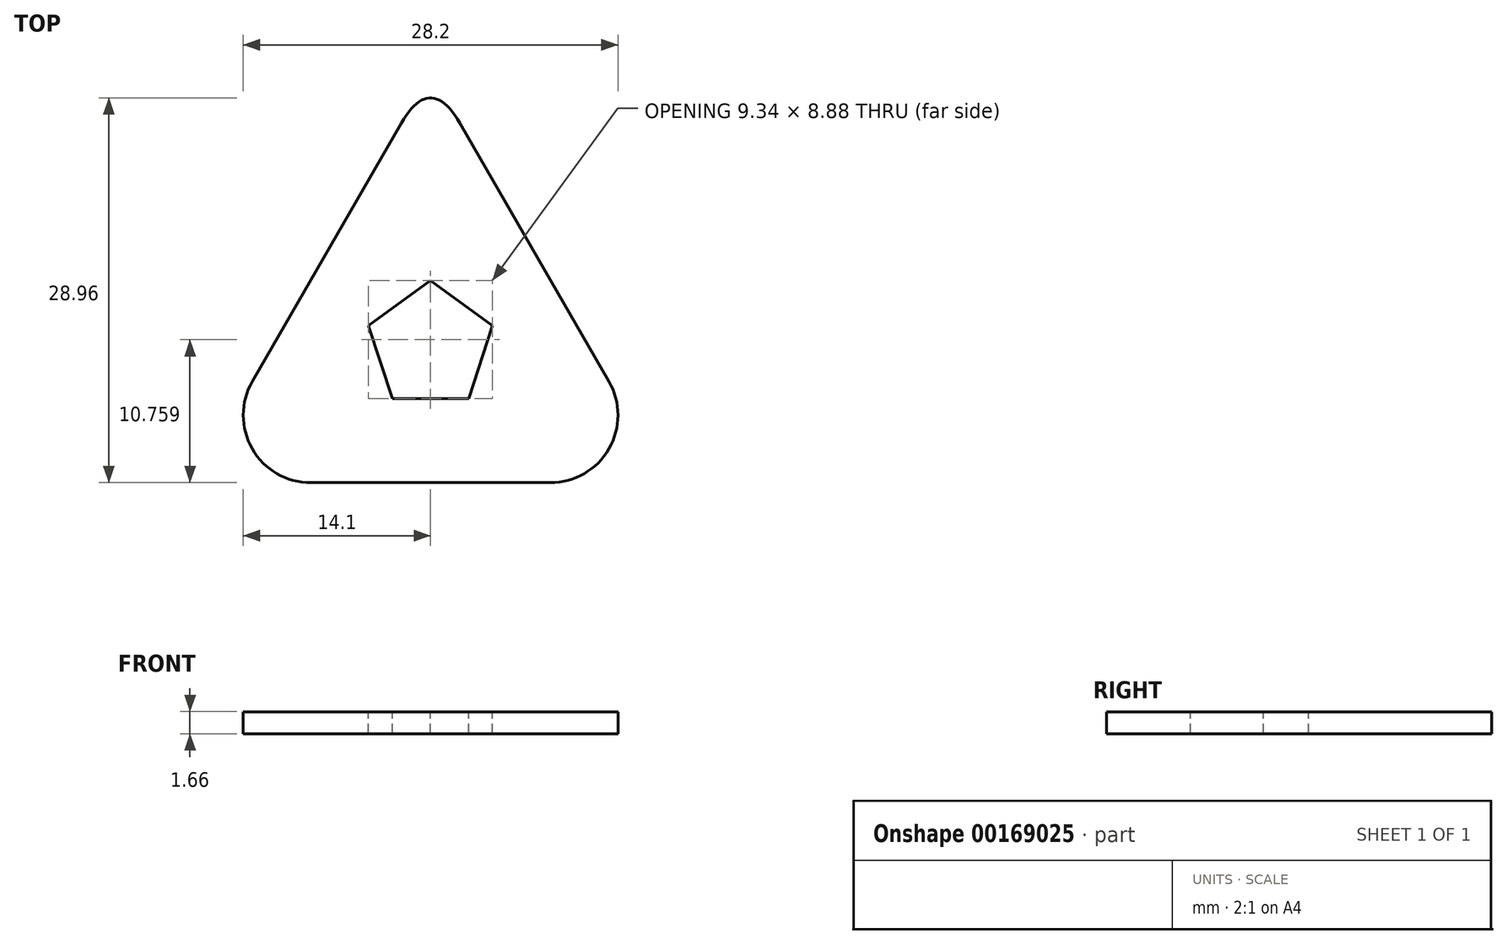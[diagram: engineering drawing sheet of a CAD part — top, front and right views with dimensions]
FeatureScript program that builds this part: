
annotation { "Feature Type Name" : "Feature", "Feature Type Description" : "" }
export const myFeature = defineFeature(function(context is Context, id is Id, definition is map)
    precondition{}
    {
        {
            var Q0;
            Q0=qCreatedBy(makeId("Top.planeOp"),FACE);
            var sketch = newSketch(context, id + "F0", { "sketchPlane" : qUnion([Q0])});
            skCircle(sketch, "E0.cCircle", {"center": v(0, 0) * mm, "radius": 20.58 * mm, "construction": true});
            skLineSegment(sketch, "E0.0", {"start": v(0, 20.58) * mm, "end": v(17.82, -10.29) * mm});
            skLineSegment(sketch, "E0.1", {"start": v(17.82, -10.29) * mm, "end": v(-17.82, -10.29) * mm});
            skLineSegment(sketch, "E0.2", {"start": v(-17.82, -10.29) * mm, "end": v(0, 20.58) * mm});
            skSolve(sketch);
        }
        {
            var Q0;
            Q0=makeQuery(id+"F0.imprint","IMPRINT",FACE,{"disambiguationData":[TD([[makeQuery(id+"F0.imprint","IMPRINT",EDGE,{"derivedFrom":sQuery(id+"F0.wireOp",EDGE,"E0.0")}),-1.0]])]});
            var Q1;
            Q1=sQuery(id+"F0.wireOp",EDGE,"E0.1");
            var Q2;
            Q2=sQuery(id+"F0.wireOp",EDGE,"E0.0");
            var Q3;
            Q3=sQuery(id+"F0.wireOp",EDGE,"E0.2");
            extrude(context, id + "F1", {"entities" : qUnion([Q0]), "surfaceEntities" : qUnion([Q1, Q2, Q3]), "depth" : 1.66 * mm});
        }
        {
            var Q0;
            Q0=makeQuery(id+"F1.opExtrude","SWEPT_EDGE",EDGE,{"disambiguationData":[OSD([sQuery(id+"F0.wireOp",EDGE,"E0.0"),sQuery(id+"F0.wireOp",EDGE,"E0.2")])]});
            fillet(context, id + "F2", {"entities" : qUnion([Q0]), "radius" : 2.54 * mm, "tangentPropagation" : true, "rho" : 0.5, "crossSection" : FilletCrossSection.CONIC, "allowEdgeOverflow" : false});
        }
        {
            var Q0;
            Q0=makeQuery(id+"F1.opExtrude","SWEPT_EDGE",EDGE,{"disambiguationData":[OSD([sQuery(id+"F0.wireOp",EDGE,"E0.1"),sQuery(id+"F0.wireOp",EDGE,"E0.2")])]});
            fillet(context, id + "F3", {"entities" : qUnion([Q0]), "radius" : 5.08 * mm, "tangentPropagation" : true, "allowEdgeOverflow" : false});
        }
        {
            var Q0;
            Q0=makeQuery(id+"F1.opExtrude","SWEPT_EDGE",EDGE,{"disambiguationData":[OSD([sQuery(id+"F0.wireOp",EDGE,"E0.0"),sQuery(id+"F0.wireOp",EDGE,"E0.1")])]});
            fillet(context, id + "F4", {"entities" : qUnion([Q0]), "radius" : 5.08 * mm, "tangentPropagation" : true, "allowEdgeOverflow" : false});
        }
        {
            var Q0;
            Q0=makeQuery(id+"F1.opExtrude","CAP_FACE",FACE,{"disambiguationData":[OSD([sQuery(id+"F0.wireOp",EDGE,"E0.0"),sQuery(id+"F0.wireOp",EDGE,"E0.1"),sQuery(id+"F0.wireOp",EDGE,"E0.2")])],"isStart":false});
            var sketch = newSketch(context, id + "F5", { "sketchPlane" : qUnion([Q0])});
            skCircle(sketch, "E1.cCircle", {"center": v(0, 0) * mm, "radius": 4.91 * mm, "construction": true});
            skLineSegment(sketch, "E1.0", {"start": v(0, 4.91) * mm, "end": v(4.67, 1.52) * mm});
            skLineSegment(sketch, "E1.1", {"start": v(4.67, 1.52) * mm, "end": v(2.89, -3.97) * mm});
            skLineSegment(sketch, "E1.2", {"start": v(2.89, -3.97) * mm, "end": v(-2.89, -3.97) * mm});
            skLineSegment(sketch, "E1.3", {"start": v(-2.89, -3.97) * mm, "end": v(-4.67, 1.52) * mm});
            skLineSegment(sketch, "E1.4", {"start": v(-4.67, 1.52) * mm, "end": v(0, 4.91) * mm});
            skSolve(sketch);
        }
        {
            var Q0;
            Q0=makeQuery(id+"F5.imprint","IMPRINT",FACE,{"disambiguationData":[TD([[makeQuery(id+"F5.imprint","IMPRINT",EDGE,{"derivedFrom":sQuery(id+"F5.wireOp",EDGE,"E1.0")}),-1.0]])]});
            extrude(context, id + "F6", {"entities" : qUnion([Q0]), "operationType" : NewBodyOperationType.REMOVE, "oppositeDirection" : true, "depth" : 25.4 * mm});
        }
    });
